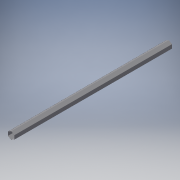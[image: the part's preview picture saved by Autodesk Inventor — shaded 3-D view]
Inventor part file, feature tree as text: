
AUTODESK INVENTOR PART (.ipt)
format: ipt  version: 2017 (Build 210142000, 142)  size: 115,200 bytes
history: native  units: mm
features: extrude x1, fillet x1, sketch x1
ambient origin geometry x8: Origin, YZ Plane, XZ Plane, XY Plane, X Axis, Y Axis, Z Axis, Center Point
bodies: Solid1 (feature_tree)
feature tree (3):
  extrude  "Extrusion1"  Depth=4.9mm
  fillet  "Fillet1"  Radius=120.0mm
  sketch  "Sketch1"  dims[d0=5.0mm d1=4.9mm d2=120.0mm d3=0.0mm d4=0.1mm]
